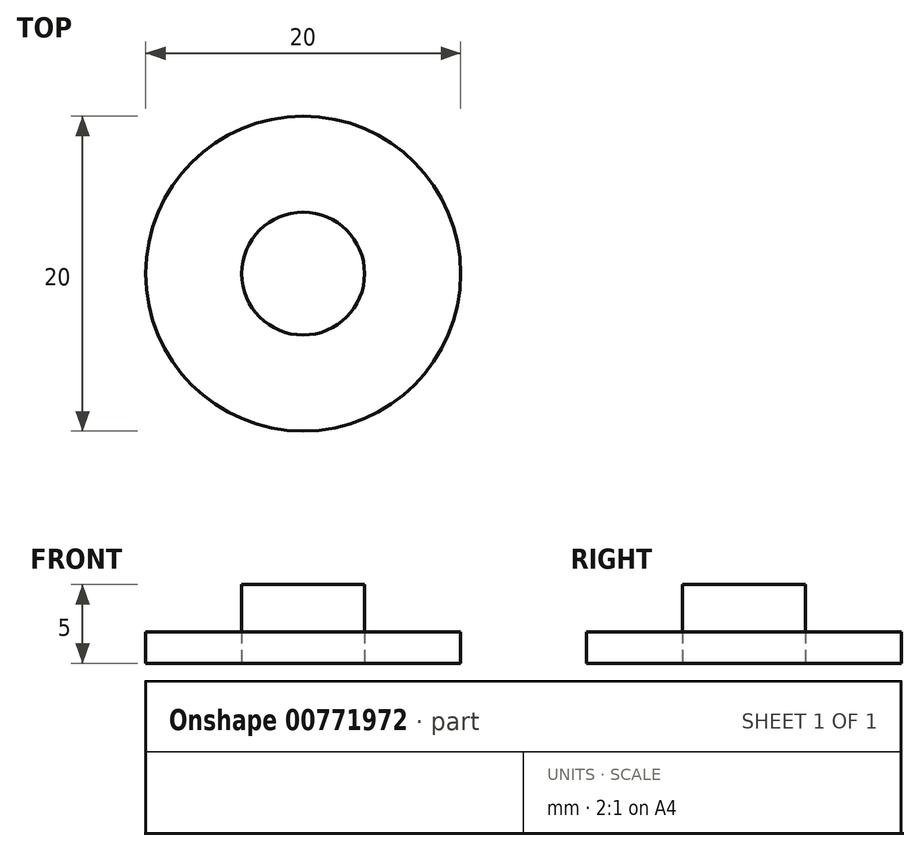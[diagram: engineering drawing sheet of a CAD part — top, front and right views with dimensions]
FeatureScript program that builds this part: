
annotation { "Feature Type Name" : "Feature", "Feature Type Description" : "" }
export const myFeature = defineFeature(function(context is Context, id is Id, definition is map)
    precondition{}
    {
        {
            var Q0;
            Q0=qCreatedBy(makeId("Top.planeOp"),FACE);
            var sketch = newSketch(context, id + "F0", { "sketchPlane" : qUnion([Q0])});
            skCircle(sketch, "E0", {"center": v(0, 0) * mm, "radius": 10 * mm});
            skSolve(sketch);
        }
        {
            var Q0;
            Q0=qCreatedBy(makeId("Top.planeOp"),FACE);
            var sketch = newSketch(context, id + "F1", { "sketchPlane" : qUnion([Q0])});
            skCircle(sketch, "E1", {"center": v(0, 0) * mm, "radius": 3.9 * mm});
            skSolve(sketch);
        }
        {
            var Q0;
            Q0=makeQuery(id+"F0.imprint","IMPRINT",FACE,{"disambiguationData":[TD([[makeQuery(id+"F0.imprint","IMPRINT",EDGE,{"derivedFrom":sQuery(id+"F0.wireOp",EDGE,"E0")}),1.0]])]});
            extrude(context, id + "F2", {"entities" : qUnion([Q0]), "depth" : 2 * mm, "offsetDistance" : 25 * mm});
        }
        {
            var Q0;
            Q0=makeQuery(id+"F1.imprint","IMPRINT",FACE,{"disambiguationData":[TD([[makeQuery(id+"F1.imprint","IMPRINT",EDGE,{"derivedFrom":sQuery(id+"F1.wireOp",EDGE,"E1")}),1.0]])]});
            extrude(context, id + "F3", {"entities" : qUnion([Q0]), "depth" : 5 * mm, "offsetDistance" : 25 * mm});
        }
    });
